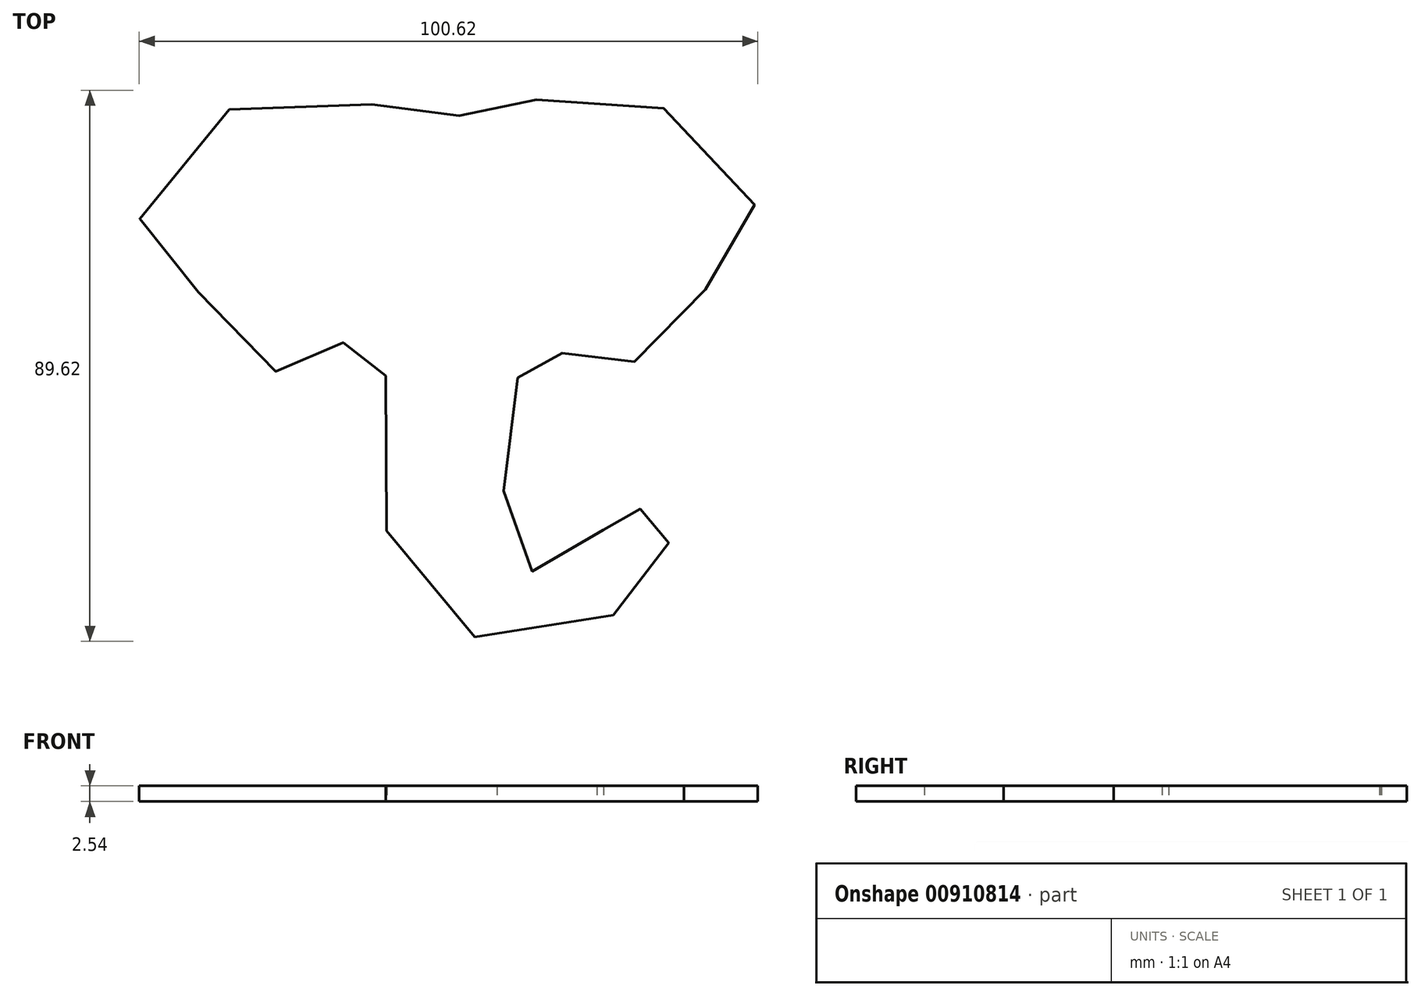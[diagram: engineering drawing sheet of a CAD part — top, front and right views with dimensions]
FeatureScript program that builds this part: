
annotation { "Feature Type Name" : "Feature", "Feature Type Description" : "" }
export const myFeature = defineFeature(function(context is Context, id is Id, definition is map)
    precondition{}
    {
        {
            var Q0;
            Q0=qCreatedBy(makeId("Top.planeOp"),FACE);
            var sketch = newSketch(context, id + "F0", { "sketchPlane" : qUnion([Q0])});
            skFitSpline(sketch, "E0", {"points": [v(74.43, 114.01) * mm, v(68.62, 113.68) * mm, v(64.46, 114.12) * mm, v(57.9, 116.64) * mm, v(43.55, 117.4) * mm, v(29.2, 109.08) * mm, v(22.63, 98.24) * mm, v(23.84, 91.56) * mm, v(30.4, 85.98) * mm, v(32.49, 85) * mm, v(36, 80.4) * mm, v(44.2, 72.62) * mm, v(50.45, 70.54) * mm, v(53.73, 73.17) * mm, v(56.14, 78.1) * mm, v(58.53, 79.34) * mm, v(61.2, 77.06) * mm, v(62.5, 70.87) * mm, v(62.53, 55.26) * mm, v(64.35, 39.11) * mm, v(74.72, 29.93) * mm, v(88.97, 29) * mm, v(100.42, 33.49) * mm, v(105, 40.15) * mm, v(107, 44.1) * mm, v(109.56, 44.87) * mm, v(110.95, 47.04) * mm, v(107.24, 48.98) * mm, v(104.3, 49.75) * mm, v(99.26, 52.54) * mm, v(96.86, 50.83) * mm, v(97.8, 47.9) * mm, v(96.79, 43.86) * mm, v(92.76, 40.3) * mm, v(86.64, 39.84) * mm, v(81.6, 42.55) * mm, v(80.76, 48.98) * mm, v(82.54, 56.64) * mm, v(83.71, 66.41) * mm, v(84.18, 73.41) * mm, v(86.14, 77.97) * mm, v(89.59, 77.58) * mm, v(91.7, 74.19) * mm, v(94.66, 70.57) * mm, v(99.48, 72) * mm, v(106.82, 76.92) * mm, v(109.88, 81.3) * mm, v(115.6, 86.56) * mm, v(121.47, 91.25) * mm, v(122.77, 98.28) * mm, v(116.91, 108.57) * mm, v(106.93, 115.53) * mm, v(94.5, 118.1) * mm, v(85.75, 116.17) * mm, v(81.6, 114.6) * mm, v(79.86, 113.87) * mm, v(74.43, 114.01) * mm]});
            skSolve(sketch);
        }
        {
            var Q0;
            Q0 = qSketchRegion(id + "F0", true);
            extrude(context, id + "F1", {"entities" : qUnion([Q0]), "depth" : 2.54 * mm, "offsetDistance" : 25.4 * mm});
        }
    });
